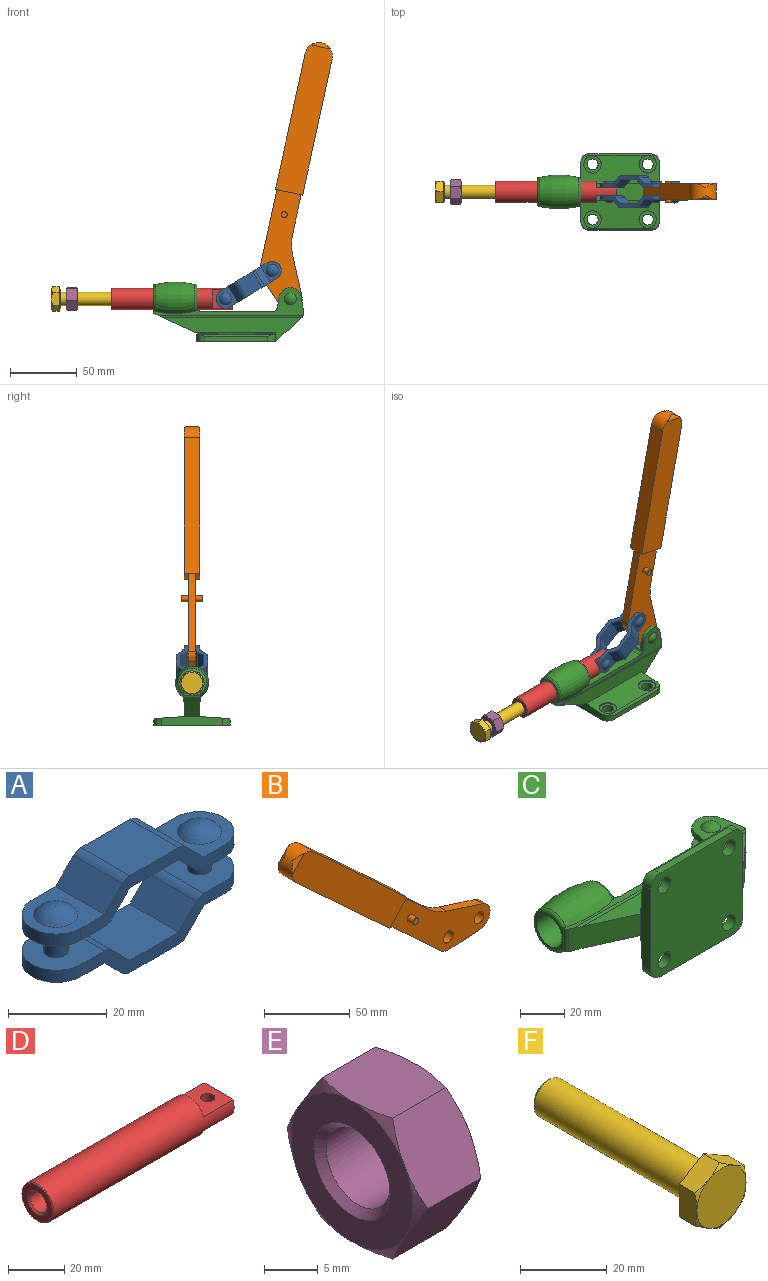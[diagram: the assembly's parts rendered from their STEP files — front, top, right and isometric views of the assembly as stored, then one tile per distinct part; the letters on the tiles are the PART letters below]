
ASSEMBLY  parts=6 mates=8
PART A: 44 faces, bbox 55x14x24 mm
  f0: plane 14x12.76mm, normal (0,0,-1), area 103.5mm2, adj f2,f29,f30,f31,f36
  f1: cylinder r=3mm len=14mm, axis (0,1,0), area 33mm2, adj f5,f29,f31,f41
  f2: plane 14x5.12mm, normal (0.71,0,-0.71), area 101.4mm2, adj f0,f29,f31,f35
  f3: plane 14x13.76mm, normal (0,0,1), area 151.9mm2, adj f4,f7,f29,f31,f38
  f4: cylinder r=7mm len=14mm, axis (0,0,-1), area 66mm2, adj f3,f6,f29,f31
  f5: plane 14x12.76mm, normal (0,0,1), area 137.9mm2, adj f1,f9,f29,f30,f31
  f6: plane 14x13.76mm, normal (0,0,-1), area 117.5mm2, adj f4,f29,f31,f32,f42
  f7: cylinder r=2.5mm len=6mm, axis (0,0,1), area 94.2mm2, adj f3,f28
  f8: sphere r=5.87mm, area 77.5mm2, adj f22
  f9: cylinder r=2.5mm len=6mm, axis (0,0,1), area 94.2mm2, adj f5,f23
  f10: sphere r=5.87mm, area 77.5mm2, adj f16
  f11: cylinder r=3mm len=14mm, axis (0,1,0), area 33mm2, adj f12,f24,f26,f28
  f12: plane 14x5.12mm, normal (0.71,0,-0.71), area 101.4mm2, adj f11,f13,f24,f26
  f13: plane 14x14mm, normal (0,0,-1), area 196mm2, adj f12,f14,f24,f26
  f14: plane 14x5.12mm, normal (-0.71,0,-0.71), area 101.4mm2, adj f13,f15,f24,f26
  f15: cylinder r=3mm len=14mm, axis (0,1,0), area 33mm2, adj f14,f23,f24,f26
  f16: plane 14x12.76mm, normal (0,0,1), area 94mm2, adj f10,f17,f24,f25,f26
  f17: plane 14x5.12mm, normal (0.71,0,0.71), area 101.4mm2, adj f16,f18,f24,f26
  f18: cylinder r=3mm len=14mm, axis (0,1,0), area 33mm2, adj f17,f19,f24,f26
  f19: plane 14x14mm, normal (0,0,1), area 196mm2, adj f18,f20,f24,f26
  f20: cylinder r=3mm len=14mm, axis (0,1,0), area 33mm2, adj f19,f21,f24,f26
  f21: plane 14x5.12mm, normal (-0.71,0,0.71), area 101.4mm2, adj f20,f22,f24,f26
  f22: plane 14x13.76mm, normal (0,0,1), area 108mm2, adj f8,f21,f24,f26,f27
  f23: plane 14x12.76mm, normal (0,0,-1), area 137.9mm2, adj f9,f15,f24,f25,f26
  f24: plane 41x9mm, normal (0,1,0), area 137.1mm2, adj f11,f12,f13,f14,f15,f16,f17,f18
  f25: cylinder r=7mm len=14mm, axis (0,0,1), area 66mm2, adj f16,f23,f24,f26
  f26: plane 41x9mm, normal (0,-1,0), area 137.1mm2, adj f11,f12,f13,f14,f15,f16,f17,f18
  f27: cylinder r=7mm len=14mm, axis (0,0,1), area 66mm2, adj f22,f24,f26,f28
  f28: plane 14x13.76mm, normal (0,0,-1), area 151.9mm2, adj f7,f11,f24,f26,f27
  f29: plane 41x9mm, normal (0,1,0), area 137.1mm2, adj f0,f1,f2,f3,f4,f5,f6,f30
  f30: cylinder r=7mm len=14mm, axis (0,0,-1), area 66mm2, adj f0,f5,f29,f31
  f31: plane 41x9mm, normal (0,-1,0), area 137.1mm2, adj f0,f1,f2,f3,f4,f5,f6,f30
  f32: plane 14x5.12mm, normal (-0.71,0,-0.71), area 101.4mm2, adj f6,f29,f31,f33
  f33: cylinder r=3mm len=14mm, axis (0,1,0), area 33mm2, adj f29,f31,f32,f34
  f34: plane 14x14mm, normal (0,0,-1), area 196mm2, adj f29,f31,f33,f35
  f35: cylinder r=3mm len=14mm, axis (0,1,0), area 33mm2, adj f2,f29,f31,f34
  f36: cylinder r=4.15mm len=8.3mm, axis (0,0,1), area 39.1mm2, adj f0,f37
  f37: plane 8.3x8.3mm, normal (0,0,-1), area 54.1mm2, adj f36
  f38: cylinder r=3mm len=14mm, axis (0,1,0), area 33mm2, adj f3,f29,f31,f39
  f39: plane 14x5.12mm, normal (0.71,0,0.71), area 101.4mm2, adj f29,f31,f38,f40
  f40: plane 14x14mm, normal (0,0,1), area 196mm2, adj f29,f31,f39,f41
  f41: plane 14x5.12mm, normal (-0.71,0,0.71), area 101.4mm2, adj f1,f29,f31,f40
  f42: cylinder r=4.15mm len=8.3mm, axis (0,0,1), area 39.1mm2, adj f6,f43
  f43: plane 8.3x8.3mm, normal (0,0,-1), area 54.1mm2, adj f42
PART B: 25 faces, bbox 167.9x15.9x133.3 mm
  f0: cylinder r=3mm len=12.74mm, axis (0.68,0,0.73), area 34.3mm2, adj f7,f11
  f1: cylinder r=3mm len=12.74mm, axis (0.68,0,0.73), area 34.3mm2, adj f7,f8
  f2: cone r=2.35mm half-angle=45deg, axis (0,1,0), area 4mm2, adj f3,f18
  f3: cylinder r=2.35mm len=4.76mm, axis (0,1,0), area 70.3mm2, adj f2,f4
  f4: plane 84.96x56.99mm, normal (0,-1,0), area 1745.8mm2, adj f3,f6,f9,f13,f14,f19,f20,f21
  f5: plane 84.96x56.99mm, normal (0,1,0), area 1745.8mm2, adj f6,f9,f13,f14,f17,f19,f20,f21
  f6: plane 15.29x14.11mm, normal (0.73,0,-0.68), area 138mm2, adj f4,f5,f8,f9,f10,f11,f12,f24
  f7: cylinder r=10.35mm len=17.95mm, axis (0,-1,0), area 341.6mm2, adj f0,f1,f8,f10,f11,f12
  f8: plane 94.12x88.79mm, normal (0,1,0), area 2304.4mm2, adj f1,f6,f7,f10,f12
  f9: plane 44.27x40.85mm, normal (-0.68,0,-0.73), area 361.4mm2, adj f4,f5,f6,f19
  f10: plane 76.69x70.84mm, normal (-0.68,0,-0.73), area 1252.8mm2, adj f6,f7,f8,f11
  f11: plane 94.12x88.79mm, normal (0,-1,0), area 2304.4mm2, adj f0,f6,f7,f10,f12
  f12: plane 76.76x70.76mm, normal (0.68,0,0.74), area 1252.8mm2, adj f6,f7,f8,f11
  f13: cylinder r=4mm len=8mm, axis (0,1,0), area 150.8mm2, adj f4,f5
  f14: cylinder r=4mm len=8mm, axis (0,1,0), area 150.8mm2, adj f4,f5
  f15: plane 4.3x4.3mm, normal (0,1,0), area 14.5mm2, adj f16
  f16: cone r=2.15mm half-angle=45deg, axis (0,-1,0), area 4mm2, adj f15,f17
  f17: cylinder r=2.35mm len=4.76mm, axis (0,1,0), area 70.3mm2, adj f5,f16
  f18: plane 4.3x4.3mm, normal (0,-1,0), area 14.5mm2, adj f2
  f19: cylinder r=9.3mm len=6.78mm, axis (0,-1,0), area 44.4mm2, adj f4,f5,f9,f20
  f20: plane 25.37x6mm, normal (0.05,0,-1), area 152.4mm2, adj f4,f5,f19,f21
  f21: cylinder r=9mm len=17.56mm, axis (0,-1,0), area 150.1mm2, adj f4,f5,f20,f22
  f22: plane 29.58x9.49mm, normal (0.31,0,0.95), area 186.4mm2, adj f4,f5,f21,f23
  f23: cylinder r=40mm len=14.91mm, axis (0,-1,0), area 104.3mm2, adj f4,f5,f22,f24
  f24: plane 21.61x19.94mm, normal (0.68,0,0.73), area 176.4mm2, adj f4,f5,f6,f23
PART C: 56 faces, bbox 157.3x88.4x101.1 mm
  f0: cylinder r=5mm len=109.05mm, axis (1,0,0), area 169.5mm2, adj f14,f20,f22,f33,f34
  f1: plane 157.27x64.79mm, normal (0,0,1), area 537.5mm2, adj f2,f12,f20,f21,f23,f24,f25,f26
  f2: torus R=9.04mm, axis (1,0,0), area 134.2mm2, adj f1,f33,f44,f45
  f3: cylinder r=6.5mm len=13mm, axis (0,1,0), area 29.6mm2, adj f42,f50,f55
  f4: cylinder r=4.15mm len=8.3mm, axis (0,1,0), area 125.2mm2, adj f5,f17
  f5: plane 13x13mm, normal (0,1,0), area 78.6mm2, adj f4,f6
  f6: cylinder r=6.5mm len=13mm, axis (0,1,0), area 29.6mm2, adj f5,f7,f43
  f7: cylinder r=1.5mm len=54.51mm, axis (1,0,0), area 115mm2, adj f6,f8,f9,f10,f43,f48
  f8: cylinder r=6.5mm len=13mm, axis (0,1,0), area 29.6mm2, adj f7,f15,f43
  f9: cylinder r=6mm len=6mm, axis (0,1,0), area 45.7mm2, adj f7,f17,f41,f43,f48
  f10: cylinder r=6mm len=6mm, axis (0,1,0), area 45.7mm2, adj f7,f17,f19,f43,f48
  f11: cylinder r=6mm len=6mm, axis (0,1,0), area 45.7mm2, adj f17,f19,f42,f49,f50
  f12: cylinder r=5mm len=109.05mm, axis (1,0,0), area 169.5mm2, adj f1,f13,f20,f22,f34
  f13: plane 104.3x17.87mm, normal (0,0,1), area 1000.4mm2, adj f12,f18,f19,f20,f22,f41,f42
  f14: plane 104.3x17.87mm, normal (0,0,-1), area 1000.4mm2, adj f0,f18,f19,f20,f22,f41,f43
  f15: plane 13x13mm, normal (0,1,0), area 78.6mm2, adj f8,f16
  f16: cylinder r=4.15mm len=8.3mm, axis (0,1,0), area 125.2mm2, adj f15,f17
  f17: plane 58.8x57.2mm, normal (0,-1,0), area 3116mm2, adj f4,f9,f10,f11,f16,f19,f41,f47
  f18: cylinder r=2mm len=12mm, axis (0,0,1), area 14.9mm2, adj f13,f14,f22,f41
  f19: plane 45.2x6.5mm, normal (-1,0,0), area 273.1mm2, adj f10,f11,f13,f14,f17,f20,f42,f43
  f20: plane 31.87x14.41mm, normal (-0.41,-0.91,0), area 421.1mm2, adj f0,f1,f12,f13,f14,f19,f21,f33
  f21: cylinder r=2mm len=12.5mm, axis (0,0,1), area 28.7mm2, adj f1,f20,f23,f33
  f22: plane 19.14x17.74mm, normal (0.68,-0.73,0), area 313.2mm2, adj f0,f12,f13,f14,f18,f34
  f23: plane 18.35x18.08mm, normal (-1,0,0), area 71.3mm2, adj f1,f21,f31,f33,f40
  f24: cylinder r=3mm len=12.5mm, axis (0,0,1), area 47.6mm2, adj f1,f25,f31,f33,f45
  f25: plane 54.31x12.5mm, normal (0,1,0), area 678.9mm2, adj f1,f24,f29,f33
  f26: plane 13.17x12.5mm, normal (0.98,0.17,0), area 105.8mm2, adj f1,f28,f30,f33,f34,f38,f39,f46
  f27: plane 12.5x8.3mm, normal (-0.98,0.17,0), area 54.9mm2, adj f1,f28,f29,f30,f33,f38,f39,f46
  f28: cylinder r=8.5mm len=16.22mm, axis (0,0,1), area 71.1mm2, adj f1,f26,f27,f39
  f29: cylinder r=3mm len=12.5mm, axis (0,0,1), area 52.4mm2, adj f1,f25,f27,f33
  f30: plane 19.45x6mm, normal (0,1,0), area 116.7mm2, adj f26,f27,f38,f39
  f31: cylinder r=7.95mm len=33mm, axis (-1,0,0), area 1648.4mm2, adj f23,f24,f45
  f32: cylinder r=4.15mm len=8.3mm, axis (0,0,1), area 39.1mm2, adj f33,f36
  f33: plane 157.27x64.79mm, normal (0,0,-1), area 547mm2, adj f0,f2,f20,f21,f23,f24,f25,f26
  f34: cylinder r=4mm len=12.5mm, axis (0,0,1), area 49.6mm2, adj f0,f1,f12,f22,f26,f33
  f35: sphere r=5.87mm, area 77.5mm2, adj f1
  f36: plane 8.3x8.3mm, normal (0,0,-1), area 54.1mm2, adj f32
  f37: cylinder r=3.15mm len=6.3mm, axis (0,0,1), area 118.8mm2, adj f38,f39
  f38: plane 19.45x15.3mm, normal (0,0,1), area 206mm2, adj f26,f27,f30,f37,f46
  f39: plane 19.45x15.3mm, normal (0,0,-1), area 206mm2, adj f26,f27,f28,f30,f37
  f40: torus R=9.04mm, axis (1,0,0), area 134.2mm2, adj f1,f23,f33,f44
  f41: plane 45.2x6.5mm, normal (1,0,0), area 197.7mm2, adj f9,f13,f14,f17,f18,f42,f43,f47
  f42: plane 58.83x21.23mm, normal (0,1,0.07), area 977.2mm2, adj f3,f11,f13,f19,f41,f47,f50,f53
  f43: plane 58.83x21.23mm, normal (0,1,-0.07), area 977.2mm2, adj f6,f7,f8,f9,f10,f14,f19,f41
  f44: revolved ~29.92x25.45mm, area 4188.9mm2, adj f1,f2,f33,f40
  f45: plane 18.08x15.57mm, normal (1,0,0), area 44.6mm2, adj f1,f2,f24,f31,f33
  f46: cylinder r=8.5mm len=16.22mm, axis (0,0,1), area 71.1mm2, adj f26,f27,f33,f38
  f47: cylinder r=6mm len=6mm, axis (0,1,0), area 45.7mm2, adj f17,f41,f42,f49,f50
  f48: plane 46.8x3.6mm, normal (0,0,-1), area 168.3mm2, adj f7,f9,f10,f17
  f49: plane 46.8x3.6mm, normal (0,0,1), area 168.3mm2, adj f11,f17,f47,f50
  f50: cylinder r=1.5mm len=54.51mm, axis (1,0,0), area 115mm2, adj f3,f11,f42,f47,f49,f53
  f51: cylinder r=4.15mm len=8.3mm, axis (0,1,0), area 125.2mm2, adj f17,f52
  f52: plane 13x13mm, normal (0,1,0), area 78.6mm2, adj f51,f53
  f53: cylinder r=6.5mm len=13mm, axis (0,1,0), area 29.6mm2, adj f42,f50,f52
  f54: cylinder r=4.15mm len=8.3mm, axis (0,1,0), area 125.2mm2, adj f17,f55
  f55: plane 13x13mm, normal (0,1,0), area 78.6mm2, adj f3,f54
PART D: 14 faces, bbox 91.2x15.9x15.9 mm
  f0: cone r=4.19mm half-angle=61.2deg, axis (-1,0,0), area 62.9mm2, adj f10
  f1: plane 15x14.73mm, normal (0,0,1), area 201.1mm2, adj f3,f5,f6,f11,f12,f13
  f2: plane 15x14.73mm, normal (0,0,-1), area 201.1mm2, adj f4,f5,f6,f11,f12,f13
  f3: plane 14.72x4.95mm, normal (1,0,0), area 52.7mm2, adj f1,f5
  f4: plane 14.72x4.95mm, normal (1,0,0), area 52.7mm2, adj f2,f5
  f5: cylinder r=7.95mm len=90.49mm, axis (-1,0,0), area 3968.9mm2, adj f1,f2,f3,f4,f6,f7,f13
  f6: cone r=7.95mm half-angle=45deg, axis (-1,0,0), area 3.1mm2, adj f1,f2,f5,f12
  f7: cone r=7.6mm half-angle=45deg, axis (1,0,0), area 24.4mm2, adj f5,f8
  f8: plane 15.19x15.19mm, normal (-1,0,0), area 102.7mm2, adj f7,f9
  f9: cone r=5mm half-angle=45deg, axis (-1,0,0), area 33.1mm2, adj f8,f10
  f10: cylinder r=4.19mm len=43.38mm, axis (-1,0,0), area 1141.6mm2, adj f0,f9
  f11: cylinder r=2.5mm len=6mm, axis (0,0,-1), area 94.2mm2, adj f1,f2
  f12: plane 15.19x6mm, normal (1,0,0), area 88.7mm2, adj f1,f2,f6,f13
  f13: cone r=7.95mm half-angle=45deg, axis (-1,0,0), area 3.1mm2, adj f1,f2,f5,f12
PART E: 23 faces, bbox 8.4x18.5x18.5 mm
  f0: plane 9.24x8.4mm, normal (0,0,1), area 73.1mm2, adj f1,f2,f8,f9,f19,f21
  f1: plane 8.4x8mm, normal (0,0.87,0.5), area 73.1mm2, adj f0,f9,f17,f18,f19,f22
  f2: plane 8.4x8mm, normal (0,-0.87,0.5), area 73.1mm2, adj f0,f7,f8,f10,f16,f21
  f3: cone r=4.19mm half-angle=45deg, axis (1,0,0), area 33.1mm2, adj f4,f6
  f4: cylinder r=4.19mm len=8.38mm, axis (-1,0,0), area 178.3mm2, adj f3,f5
  f5: cone r=5mm half-angle=45deg, axis (-1,0,0), area 33.1mm2, adj f4,f11
  f6: plane 16x16mm, normal (1,0,0), area 122.5mm2, adj f3,f7,f13,f18,f19,f20,f21
  f7: cone r=15.27mm half-angle=60deg, axis (-1,0,0), area 4mm2, adj f2,f6,f16
  f8: cone r=8mm half-angle=60deg, axis (1,0,0), area 4mm2, adj f0,f2,f11
  f9: cone r=8mm half-angle=60deg, axis (1,0,0), area 4mm2, adj f0,f1,f11
  f10: cone r=8mm half-angle=60deg, axis (1,0,0), area 4mm2, adj f2,f11,f16
  f11: plane 16x16mm, normal (-1,0,0), area 122.5mm2, adj f5,f8,f9,f10,f12,f14,f22
  f12: cone r=8mm half-angle=60deg, axis (1,0,0), area 4mm2, adj f11,f15,f16
  f13: cone r=15.27mm half-angle=60deg, axis (-1,0,0), area 4mm2, adj f6,f15,f17
  f14: cone r=8mm half-angle=60deg, axis (1,0,0), area 4mm2, adj f11,f15,f17
  f15: plane 9.24x8.4mm, normal (0,0,-1), area 73.1mm2, adj f12,f13,f14,f16,f17,f20
  f16: plane 8.4x8mm, normal (0,-0.87,-0.5), area 73.1mm2, adj f2,f7,f10,f12,f15,f20
  f17: plane 8.4x8mm, normal (0,0.87,-0.5), area 73.1mm2, adj f1,f13,f14,f15,f18,f22
  f18: cone r=15.27mm half-angle=60deg, axis (-1,0,0), area 4mm2, adj f1,f6,f17
  f19: cone r=15.27mm half-angle=60deg, axis (-1,0,0), area 4mm2, adj f0,f1,f6
  f20: cone r=15.27mm half-angle=60deg, axis (-1,0,0), area 4mm2, adj f6,f15,f16
  f21: cone r=15.27mm half-angle=60deg, axis (-1,0,0), area 4mm2, adj f0,f2,f6
  f22: cone r=8mm half-angle=60deg, axis (1,0,0), area 4mm2, adj f1,f11,f17
PART F: 20 faces, bbox 18.5x57x18.5 mm
  f0: plane 8x5.8mm, normal (-0.5,0,0.87), area 51.3mm2, adj f2,f4,f11,f17,f18
  f1: plane 16x16mm, normal (0,-1,0), area 201.1mm2, adj f2,f3,f14,f15,f16,f17
  f2: cone r=18.05mm half-angle=60deg, axis (0,1,0), area 4mm2, adj f0,f1,f18
  f3: cone r=18.05mm half-angle=60deg, axis (0,1,0), area 4mm2, adj f1,f18,f19
  f4: plane 18.48x16mm, normal (0,1,0), area 53.6mm2, adj f0,f6,f11,f12,f13,f18,f19
  f5: plane 8.16x8.16mm, normal (0,1,0), area 52.3mm2, adj f10
  f6: cylinder r=7.32mm len=14.63mm, axis (0,1,0), area 27.6mm2, adj f4,f7
  f7: plane 14.63x14.63mm, normal (0,1,0), area 81.5mm2, adj f6,f8
  f8: torus R=5.25mm, axis (0,-1,0), area 12.6mm2, adj f7,f9
  f9: cylinder r=5mm len=49.43mm, axis (0,1,0), area 1552.9mm2, adj f8,f10
  f10: cone r=4.08mm half-angle=45deg, axis (0,-1,0), area 37.1mm2, adj f5,f9
  f11: plane 9.24x5.8mm, normal (-1,0,0), area 51.3mm2, adj f0,f4,f12,f16,f17
  f12: plane 8x5.8mm, normal (-0.5,0,-0.87), area 51.3mm2, adj f4,f11,f13,f15,f16
  f13: plane 8x5.8mm, normal (0.5,0,-0.87), area 51.3mm2, adj f4,f12,f14,f15,f19
  f14: cone r=18.05mm half-angle=60deg, axis (0,1,0), area 4mm2, adj f1,f13,f19
  f15: cone r=18.05mm half-angle=60deg, axis (0,1,0), area 4mm2, adj f1,f12,f13
  f16: cone r=18.05mm half-angle=60deg, axis (0,1,0), area 4mm2, adj f1,f11,f12
  f17: cone r=18.05mm half-angle=60deg, axis (0,1,0), area 4mm2, adj f0,f1,f11
  f18: plane 8x5.8mm, normal (0.5,0,0.87), area 51.3mm2, adj f0,f2,f3,f4,f19
  f19: plane 9.24x5.8mm, normal (1,0,0), area 51.3mm2, adj f3,f4,f13,f14,f18
PLACE A rot(axis=(0.93,-0.26,0.26),94.2deg) t=(2.75,-28.55,102.75)mm
PLACE B rot(axis=(0,1,0),59.6deg) t=(2.75,-28.55,102.75)mm
PLACE C rot(axis=(1,0,0),90deg) t=(-53.64,-28.55,49.57)mm fixed
PLACE D rot(axis=(1,0,0),90deg) t=(-118.06,-28.55,81.37)mm
PLACE E rot(axis=(1,0,0),5.2deg) t=(-151.92,-28.55,81.37)mm
PLACE F rot(axis=(0,0,-1),90deg) t=(-156.48,-28.55,81.37)mm
MATE cylindrical D.f0 <-> C.f2  axis (-1,0,0) through (-72.46,-28.55,81.37)mm
MATE planar A.f3 <-> D.f11  axis (0,-1,0) through (-31.76,-25.55,81.79)mm
MATE cylindrical F.f9 <-> D.f0  axis (1,0,0) through (-131.51,-28.55,81.37)mm
MATE planar B.f14 <-> C.f28  axis (0,-1,0) through (16.46,-31.55,81.37)mm
MATE cylindrical A.f7 <-> D.f11  axis (0,-1,0) through (-32.46,-28.55,81.37)mm
MATE cylindrical B.f14 <-> C.f28  axis (0,1,0) through (16.46,-28.55,81.37)mm
MATE cylindrical A.f9 <-> B.f13  axis (0,-1,0) through (2.75,-28.55,102.75)mm
MATE cylindrical E.f3 <-> F.f9  axis (-1,0,0) through (-147.72,-28.55,81.37)mm
